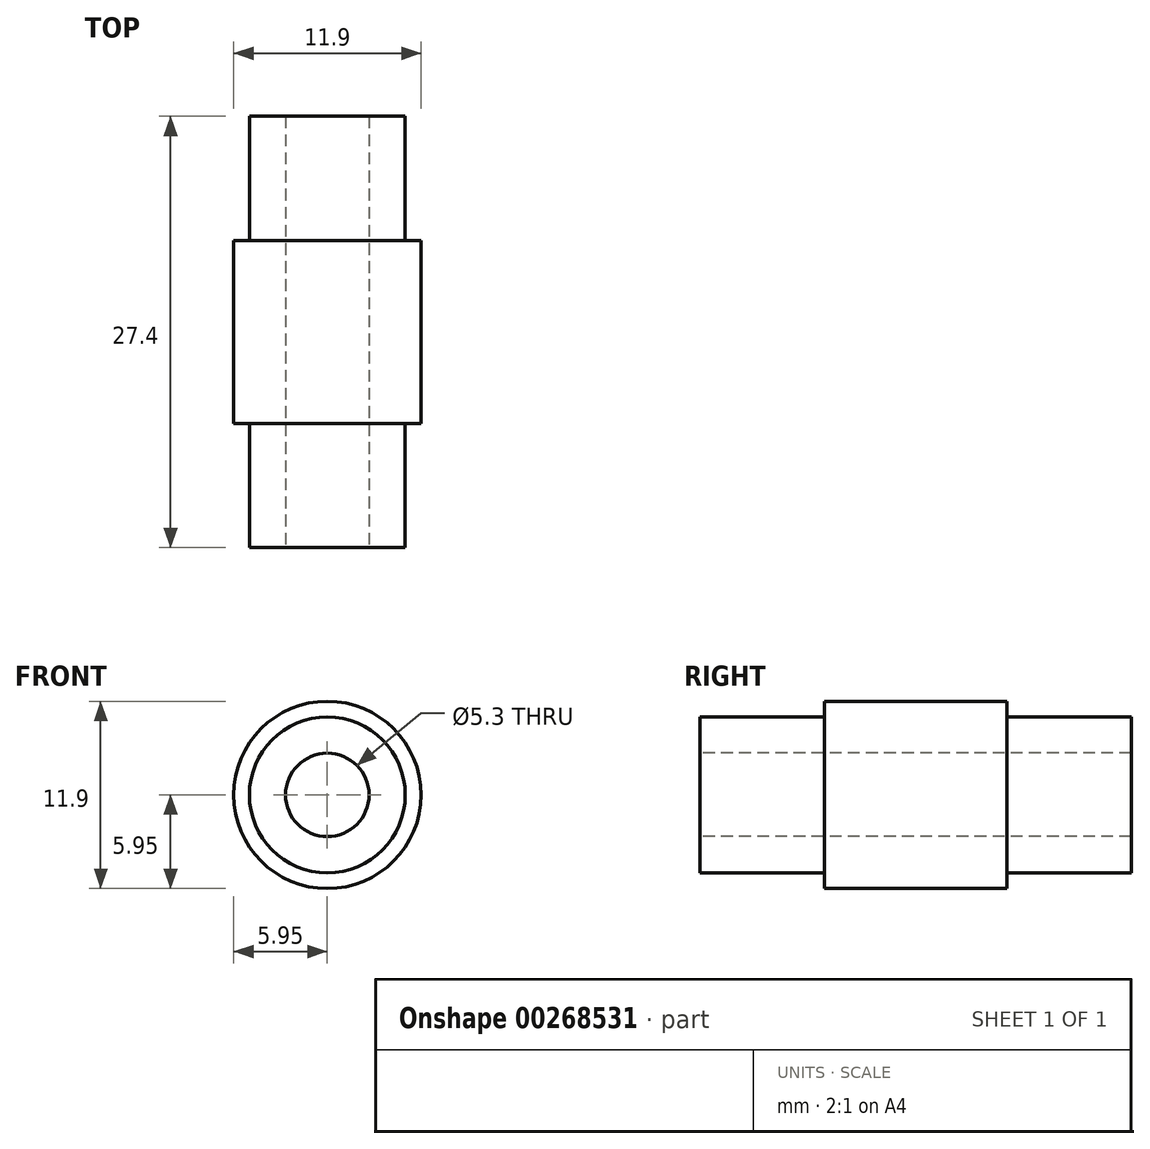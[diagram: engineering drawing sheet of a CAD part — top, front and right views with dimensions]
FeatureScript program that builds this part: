
annotation { "Feature Type Name" : "Feature", "Feature Type Description" : "" }
export const myFeature = defineFeature(function(context is Context, id is Id, definition is map)
    precondition{}
    {
        {
            var Q0;
            Q0=qCreatedBy(makeId("Front.planeOp"),FACE);
            var sketch = newSketch(context, id + "F0", { "sketchPlane" : qUnion([Q0])});
            skCircle(sketch, "E0", {"center": v(0, 0) * mm, "radius": 5.95 * mm});
            skSolve(sketch);
        }
        {
            var Q0;
            Q0 = qSketchRegion(id + "F0", true);
            extrude(context, id + "F1", {"entities" : qUnion([Q0]), "depth" : 5.8 * mm});
        }
        {
            var Q0;
            Q0=makeQuery(id+"F1.opExtrude","CAP_FACE",FACE,{"disambiguationData":[OSD([sQuery(id+"F0.wireOp",EDGE,"E0")])],"isStart":false});
            var sketch = newSketch(context, id + "F2", { "sketchPlane" : qUnion([Q0])});
            skCircle(sketch, "E1", {"center": v(0, 0) * mm, "radius": 4.95 * mm});
            skSolve(sketch);
        }
        {
            var Q0;
            Q0 = qSketchRegion(id + "F2", true);
            extrude(context, id + "F3", {"entities" : qUnion([Q0]), "operationType" : NewBodyOperationType.ADD, "depth" : 7.9 * mm});
        }
        {
            var Q0;
            Q0=makeQuery(id+"F1.opExtrude","SWEPT_BODY",BODY,{"disambiguationData":[OSD([sQuery(id+"F0.wireOp",EDGE,"E0")])]});
            var Q1;
            Q1=makeQuery(id+"F1.opExtrude","CAP_FACE",FACE,{"disambiguationData":[OSD([sQuery(id+"F0.wireOp",EDGE,"E0")])],"isStart":true});
            mirror(context, id + "F4", {"operationType" : NewBodyOperationType.ADD, "entities" : qUnion([Q0]), "mirrorPlane" : qUnion([Q1])});
        }
        {
            var Q0;
            Q0=makeQuery(id+"F3.opExtrude","CAP_FACE",FACE,{"disambiguationData":[OSD([sQuery(id+"F2.wireOp",EDGE,"E1")])],"isStart":false});
            var sketch = newSketch(context, id + "F5", { "sketchPlane" : qUnion([Q0])});
            skCircle(sketch, "E2", {"center": v(0, 0) * mm, "radius": 2.65 * mm});
            skSolve(sketch);
        }
        {
            var Q0;
            Q0 = qSketchRegion(id + "F5", true);
            extrude(context, id + "F6", {"entities" : qUnion([Q0]), "operationType" : NewBodyOperationType.REMOVE, "oppositeDirection" : true, "depth" : 35 * mm});
        }
    });
